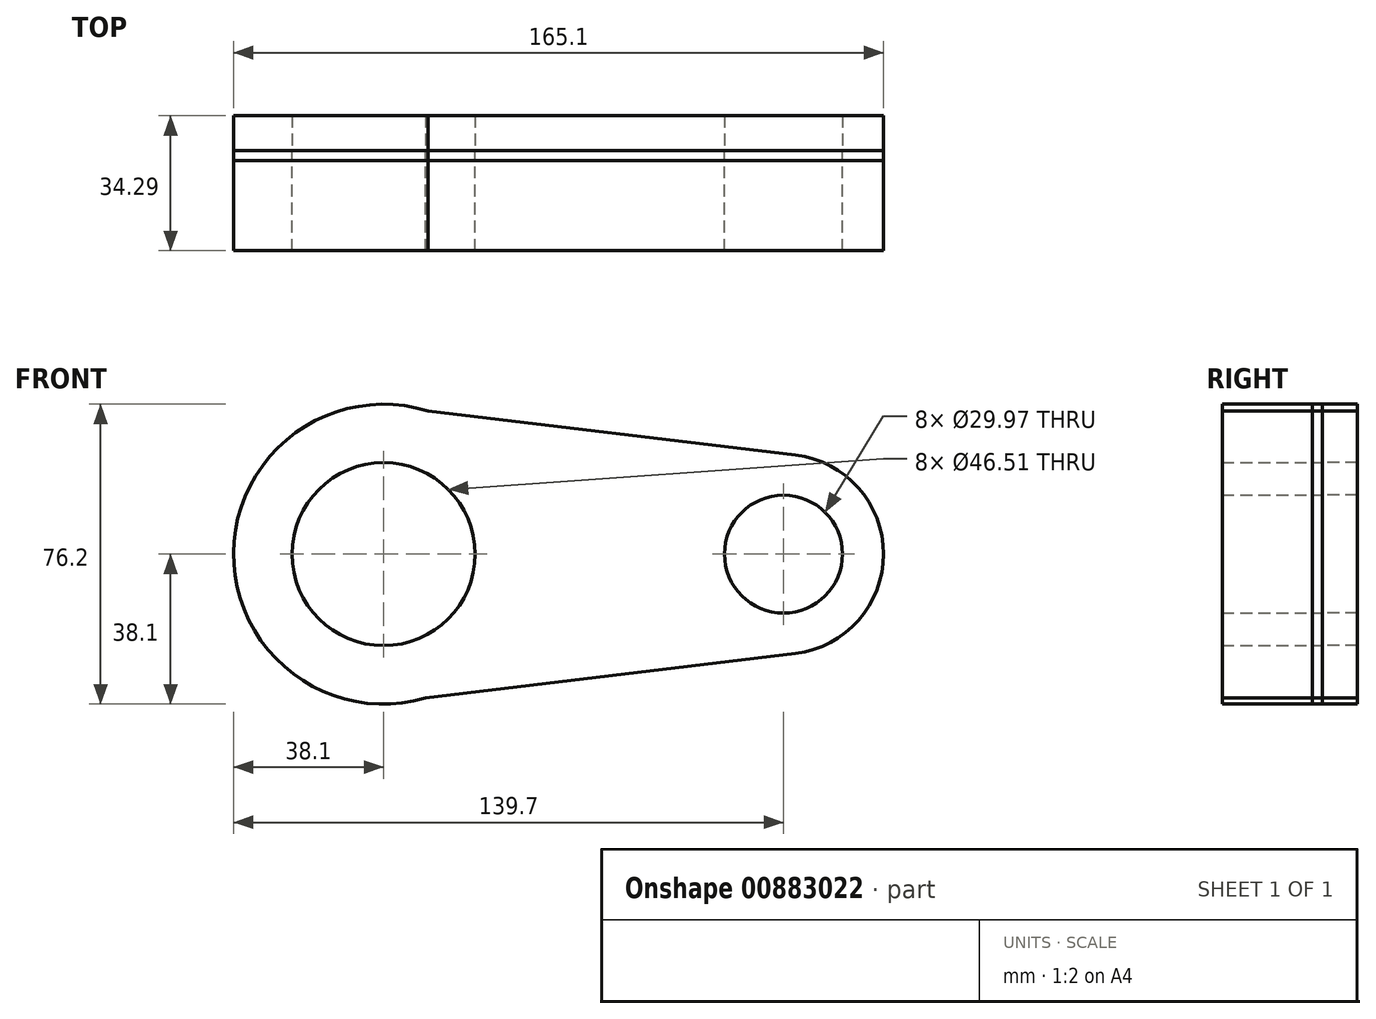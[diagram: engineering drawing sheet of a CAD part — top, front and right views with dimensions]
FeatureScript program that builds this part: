
annotation { "Feature Type Name" : "Feature", "Feature Type Description" : "" }
export const myFeature = defineFeature(function(context is Context, id is Id, definition is map)
    precondition{}
    {
        {
            var Q0;
            Q0=qCreatedBy(makeId("Front.planeOp"),FACE);
            var sketch = newSketch(context, id + "F0", { "sketchPlane" : qUnion([Q0])});
            skCircle(sketch, "E0", {"center": v(-74.44, 0) * mm, "radius": 23.26 * mm});
            skCircle(sketch, "E1", {"center": v(27.16, 0) * mm, "radius": 14.99 * mm});
            skCircle(sketch, "E2", {"center": v(-74.44, 0) * mm, "radius": 38.1 * mm});
            skCircle(sketch, "E3", {"center": v(27.16, 0) * mm, "radius": 25.4 * mm});
            skLineSegment(sketch, "E4", {"start": v(-74.44, 38.1) * mm, "end": v(-65.06, 36.93) * mm});
            skLineSegment(sketch, "E5", {"start": v(-74.44, -38.1) * mm, "end": v(-65.2, -36.96) * mm});
            skPoint(sketch, "E6.orphan", {"position": v(27.16, -25.6) * mm});
            skPoint(sketch, "E7.orphan", {"position": v(27.16, 25.4) * mm});
            skLineSegment(sketch, "E8", {"start": v(-76.01, -38.07) * mm, "end": v(30.21, -25.22) * mm});
            skLineSegment(sketch, "E9", {"start": v(-76.77, 38.03) * mm, "end": v(30.21, 25.22) * mm});
            skSolve(sketch);
        }
        {
            var Q0;
            Q0 = qSketchRegion(id + "F0", true);
            extrude(context, id + "F1", {"entities" : qUnion([Q0]), "depth" : 25.4 * mm, "offsetDistance" : 25.4 * mm});
        }
        {
            var Q0;
            Q0 = qSketchRegion(id + "F0", true);
            extrude(context, id + "F2", {"entities" : qUnion([Q0]), "oppositeDirection" : true, "depth" : 8.9 * mm, "offsetDistance" : 25.4 * mm});
        }
        {
            var Q0;
            Q0 = qSketchRegion(id + "F0", true);
            extrude(context, id + "F3", {"entities" : qUnion([Q0]), "depth" : 25.4 * mm, "offsetDistance" : 25.4 * mm});
        }
        {
            var Q0;
            Q0 = qSketchRegion(id + "F0", true);
            extrude(context, id + "F4", {"entities" : qUnion([Q0]), "depth" : 2.54 * mm, "offsetDistance" : 25.4 * mm});
        }
    });
